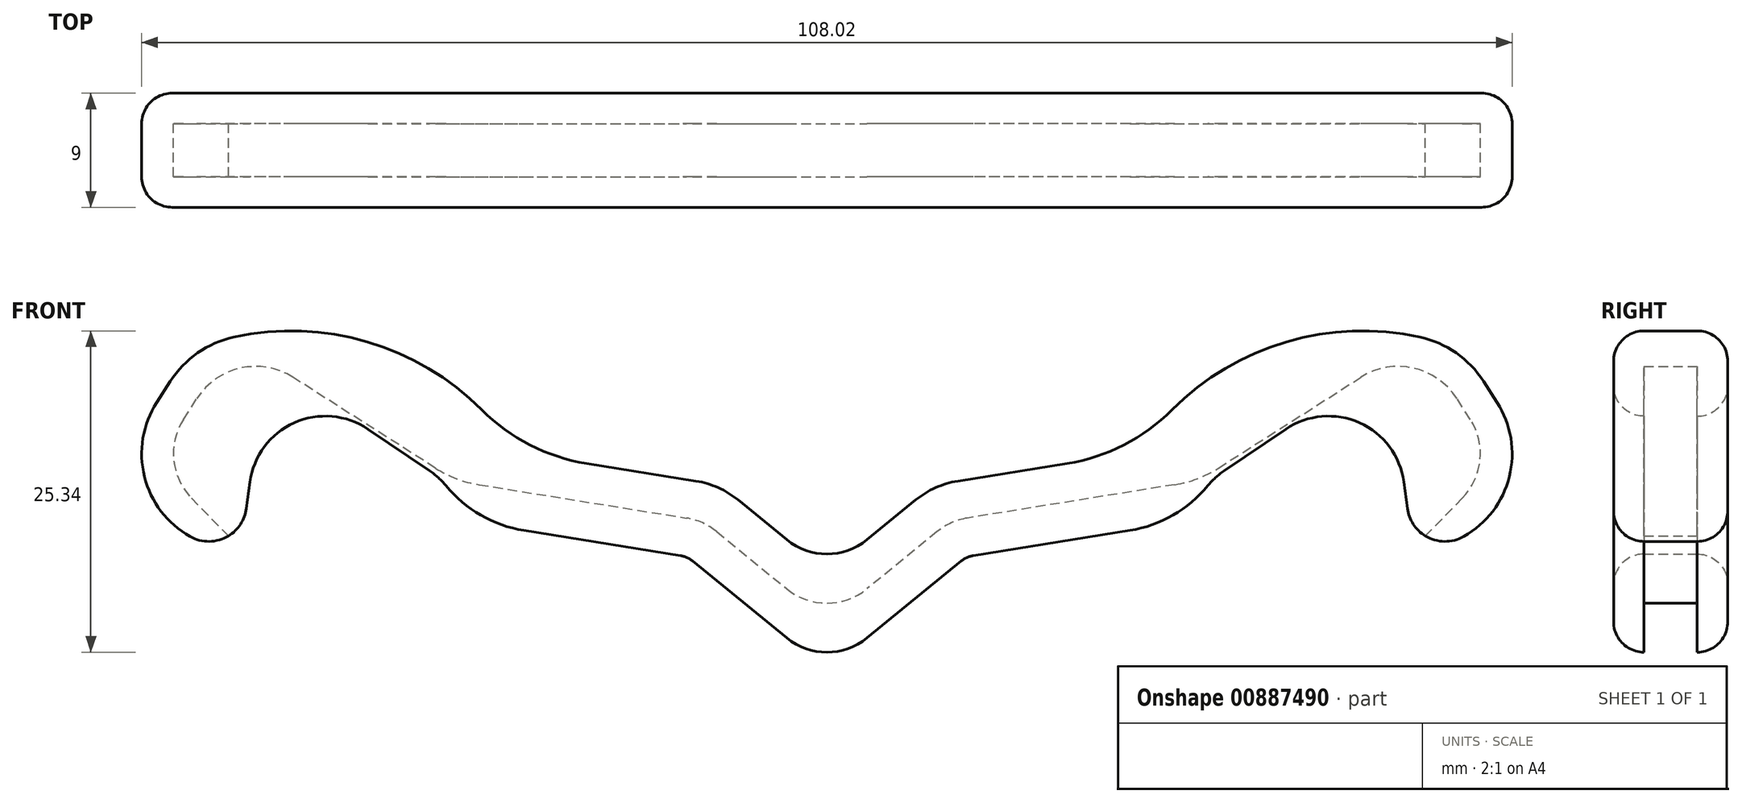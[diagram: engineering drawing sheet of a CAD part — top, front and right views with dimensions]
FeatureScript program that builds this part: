
annotation { "Feature Type Name" : "Feature", "Feature Type Description" : "" }
export const myFeature = defineFeature(function(context is Context, id is Id, definition is map)
    precondition{}
    {
        {
            var Q0;
            Q0=qCreatedBy(makeId("Front.planeOp"),FACE);
            var sketch = newSketch(context, id + "F0", { "sketchPlane" : qUnion([Q0])});
            skLineSegment(sketch, "E0.bottom", {"start": v(51.5, -38.63) * mm, "end": v(-51.5, -38.63) * mm, "construction": true});
            skLineSegment(sketch, "E0.top", {"start": v(51.5, 38.63) * mm, "end": v(-51.5, 38.63) * mm, "construction": true});
            skLineSegment(sketch, "E0.left", {"start": v(51.5, -38.63) * mm, "end": v(51.5, 38.63) * mm, "construction": true});
            skLineSegment(sketch, "E0.right", {"start": v(-51.5, -38.63) * mm, "end": v(-51.5, 38.63) * mm, "construction": true});
            skLineSegment(sketch, "E1", {"start": v(-50.1, 11.75) * mm, "end": v(-37.3, -1.35) * mm});
            skLineSegment(sketch, "E2", {"start": v(-22.41, -38.63) * mm, "end": v(-33.91, -6.75) * mm});
            skLineSegment(sketch, "E3", {"start": v(-30.84, 14.1) * mm, "end": v(-42.08, 21.26) * mm});
            skLineSegment(sketch, "E4", {"start": v(-27.43, 12.8) * mm, "end": v(-11.06, 10.17) * mm});
            skLineSegment(sketch, "E5", {"start": v(-8.7, 9.1) * mm, "end": v(-3.16, 4.6) * mm});
            skLineSegment(sketch, "E6", {"start": v(-50.72, 17.95) * mm, "end": v(-49.66, 19.6) * mm});
            skPoint(sketch, "E7.visualSharp", {"position": v(-9.74, 9.96) * mm});
            skArc(sketch, "E7.filletArc", {"start": v(-8.7, 9.1) * mm, "mid": v(-9.81, 9.8) * mm, "end": v(-11.06, 10.17) * mm});
            skPoint(sketch, "E8.visualSharp", {"position": v(-29.27, 13.1) * mm});
            skArc(sketch, "E8.filletArc", {"start": v(-30.84, 14.1) * mm, "mid": v(-29.2, 13.28) * mm, "end": v(-27.43, 12.8) * mm});
            skPoint(sketch, "E9.visualSharp", {"position": v(-52.87, 14.6) * mm});
            skArc(sketch, "E9.filletArc", {"start": v(-50.72, 17.95) * mm, "mid": v(-51.49, 14.74) * mm, "end": v(-50.1, 11.75) * mm});
            skPoint(sketch, "E10.visualSharp", {"position": v(-46.7, 24.21) * mm});
            skArc(sketch, "E10.filletArc", {"start": v(-42.08, 21.26) * mm, "mid": v(-46.21, 22) * mm, "end": v(-49.66, 19.6) * mm});
            skPoint(sketch, "E11.visualSharp", {"position": v(-35.02, -3.68) * mm});
            skArc(sketch, "E11.filletArc", {"start": v(-33.91, -6.75) * mm, "mid": v(-35.31, -3.87) * mm, "end": v(-37.3, -1.35) * mm});
            skCircle(sketch, "E12", {"center": v(-39.53, 12.21) * mm, "radius": 2 * mm});
            skCircle(sketch, "E13", {"center": v(-39.53, 12.21) * mm, "radius": 6 * mm});
            skPoint(sketch, "E14.visualSharp", {"position": v(-50.1, 11.75) * mm});
            skArc(sketch, "E15.0", {"start": v(-52.83, 19.3) * mm, "mid": v(-53.8, 13.44) * mm, "end": v(-50.21, 8.72) * mm});
            skLineSegment(sketch, "E15.1", {"start": v(-52.83, 19.3) * mm, "end": v(-51.76, 20.95) * mm});
            skArc(sketch, "E15.2", {"start": v(-40.73, 23.37) * mm, "mid": v(-46.75, 24.44) * mm, "end": v(-51.76, 20.95) * mm});
            skLineSegment(sketch, "E15.3", {"start": v(-29.5, 16.2) * mm, "end": v(-40.73, 23.37) * mm});
            skLineSegment(sketch, "E15.4", {"start": v(-7, 11.6) * mm, "end": v(-3.16, 8.46) * mm});
            skLineSegment(sketch, "E15.6", {"start": v(-18.95, 14.48) * mm, "end": v(-10.32, 13.1) * mm});
            skArc(sketch, "E15.7", {"start": v(-29.5, 16.2) * mm, "mid": v(-27.08, 15.28) * mm, "end": v(-24.49, 15.37) * mm});
            skArc(sketch, "E16", {"start": v(-27.2, 18.7) * mm, "mid": v(-36.23, 24.08) * mm, "end": v(-46.75, 24.44) * mm});
            skPoint(sketch, "E17.visualSharp", {"position": v(-24.49, 15.37) * mm});
            skArc(sketch, "E17.filletArc", {"start": v(-27.2, 18.7) * mm, "mid": v(-23.4, 15.94) * mm, "end": v(-18.95, 14.48) * mm});
            skLineSegment(sketch, "E18", {"start": v(-45.76, 10.93) * mm, "end": v(-45.48, 13) * mm});
            skPoint(sketch, "E19.visualSharp", {"position": v(-46.18, 7.75) * mm});
            skArc(sketch, "E19.filletArc", {"start": v(-50.21, 8.72) * mm, "mid": v(-47.4, 8.64) * mm, "end": v(-45.76, 10.93) * mm});
            skPoint(sketch, "E20.MirrorP", {"position": v(0, 0) * mm});
            skCircle(sketch, "E21", {"center": v(-34.67, 8.92) * mm, "radius": 2 * mm, "construction": true});
            skCircle(sketch, "E22", {"center": v(-34.67, 8.92) * mm, "radius": 6 * mm});
            skLineSegment(sketch, "E23", {"start": v(-36.17, 17.18) * mm, "end": v(-31.3, 13.9) * mm});
            skLineSegment(sketch, "E24.0", {"start": v(-10.6, 6.78) * mm, "end": v(-3.16, 0.72) * mm});
            skArc(sketch, "E24.1", {"start": v(-10.6, 6.78) * mm, "mid": v(-11.04, 7.06) * mm, "end": v(-11.54, 7.2) * mm});
            skLineSegment(sketch, "E24.2", {"start": v(-28.76, 9.98) * mm, "end": v(-11.54, 7.2) * mm});
            skArc(sketch, "E25", {"start": v(-30.03, 12.73) * mm, "mid": v(-27.28, 10.4) * mm, "end": v(-23.89, 9.2) * mm});
            skPoint(sketch, "E26.visualSharp", {"position": v(-8.47, 12.8) * mm});
            skArc(sketch, "E26.filletArc", {"start": v(-7, 11.6) * mm, "mid": v(-8.57, 12.57) * mm, "end": v(-10.32, 13.1) * mm});
            skLineSegment(sketch, "E27.MirrorCS", {"start": v(52.83, 19.3) * mm, "end": v(51.76, 20.95) * mm});
            skArc(sketch, "E28.MirrorCS", {"start": v(10.6, 6.78) * mm, "mid": v(11.04, 7.06) * mm, "end": v(11.54, 7.2) * mm});
            skLineSegment(sketch, "E29.MirrorCS", {"start": v(50.72, 17.95) * mm, "end": v(49.66, 19.6) * mm});
            skArc(sketch, "E30.MirrorCS", {"start": v(7, 11.6) * mm, "mid": v(8.57, 12.57) * mm, "end": v(10.32, 13.1) * mm});
            skArc(sketch, "E31.MirrorCS", {"start": v(8.7, 9.1) * mm, "mid": v(9.81, 9.8) * mm, "end": v(11.06, 10.17) * mm});
            skLineSegment(sketch, "E32.MirrorCS", {"start": v(45.76, 10.93) * mm, "end": v(45.48, 13) * mm});
            skArc(sketch, "E33.MirrorCS", {"start": v(33.91, -6.75) * mm, "mid": v(35.31, -3.87) * mm, "end": v(37.3, -1.35) * mm});
            skArc(sketch, "E34.MirrorCS", {"start": v(30.84, 14.1) * mm, "mid": v(29.2, 13.28) * mm, "end": v(27.43, 12.8) * mm});
            skLineSegment(sketch, "E35.MirrorCS", {"start": v(30.84, 14.1) * mm, "end": v(42.08, 21.26) * mm});
            skLineSegment(sketch, "E36.MirrorCS", {"start": v(28.76, 9.98) * mm, "end": v(11.54, 7.2) * mm});
            skLineSegment(sketch, "E37.MirrorCS", {"start": v(36.17, 17.18) * mm, "end": v(31.3, 13.9) * mm});
            skArc(sketch, "E38.MirrorCS", {"start": v(50.21, 8.72) * mm, "mid": v(47.4, 8.64) * mm, "end": v(45.76, 10.93) * mm});
            skPoint(sketch, "E39.MirrorP", {"position": v(52.87, 14.6) * mm});
            skArc(sketch, "E40.MirrorCS", {"start": v(50.72, 17.95) * mm, "mid": v(51.49, 14.74) * mm, "end": v(50.1, 11.75) * mm});
            skLineSegment(sketch, "E41.MirrorCS", {"start": v(50.1, 11.75) * mm, "end": v(37.3, -1.35) * mm});
            skPoint(sketch, "E42.MirrorP", {"position": v(9.74, 9.96) * mm});
            skArc(sketch, "E43.MirrorCS", {"start": v(29.5, 16.2) * mm, "mid": v(27.08, 15.28) * mm, "end": v(24.49, 15.37) * mm});
            skPoint(sketch, "E44.MirrorP", {"position": v(24.49, 15.37) * mm});
            skLineSegment(sketch, "E45.MirrorCS", {"start": v(27.43, 12.8) * mm, "end": v(11.06, 10.17) * mm});
            skArc(sketch, "E46.MirrorCS", {"start": v(52.83, 19.3) * mm, "mid": v(53.8, 13.44) * mm, "end": v(50.21, 8.72) * mm});
            skCircle(sketch, "E47.MirrorC", {"center": v(34.67, 8.92) * mm, "radius": 6 * mm});
            skLineSegment(sketch, "E48.MirrorCS", {"start": v(29.5, 16.2) * mm, "end": v(40.73, 23.37) * mm});
            skPoint(sketch, "E49.MirrorP", {"position": v(29.27, 13.1) * mm});
            skPoint(sketch, "E50.MirrorP", {"position": v(35.02, -3.68) * mm});
            skPoint(sketch, "E51.MirrorP", {"position": v(46.18, 7.75) * mm});
            skArc(sketch, "E52.MirrorCS", {"start": v(27.2, 18.7) * mm, "mid": v(36.23, 24.08) * mm, "end": v(46.75, 24.44) * mm});
            skPoint(sketch, "E53.MirrorP", {"position": v(8.47, 12.8) * mm});
            skCircle(sketch, "E54.MirrorC", {"center": v(39.53, 12.21) * mm, "radius": 2 * mm});
            skArc(sketch, "E55.MirrorCS", {"start": v(42.08, 21.26) * mm, "mid": v(46.21, 22) * mm, "end": v(49.66, 19.6) * mm});
            skPoint(sketch, "E56.MirrorP", {"position": v(50.1, 11.75) * mm});
            skLineSegment(sketch, "E57.MirrorCS", {"start": v(18.95, 14.48) * mm, "end": v(10.32, 13.1) * mm});
            skLineSegment(sketch, "E58.MirrorCS", {"start": v(10.6, 6.78) * mm, "end": v(3.16, 0.72) * mm});
            skCircle(sketch, "E59.MirrorC", {"center": v(34.67, 8.92) * mm, "radius": 2 * mm, "construction": true});
            skArc(sketch, "E60.MirrorCS", {"start": v(30.03, 12.73) * mm, "mid": v(27.28, 10.4) * mm, "end": v(23.89, 9.2) * mm});
            skLineSegment(sketch, "E61.MirrorCS", {"start": v(7, 11.6) * mm, "end": v(3.16, 8.46) * mm});
            skLineSegment(sketch, "E62.MirrorCS", {"start": v(8.7, 9.1) * mm, "end": v(3.16, 4.6) * mm});
            skPoint(sketch, "E63.MirrorP", {"position": v(46.7, 24.21) * mm});
            skCircle(sketch, "E64.MirrorC", {"center": v(39.53, 12.21) * mm, "radius": 6 * mm});
            skArc(sketch, "E65.MirrorCS", {"start": v(27.2, 18.7) * mm, "mid": v(23.4, 15.94) * mm, "end": v(18.95, 14.48) * mm});
            skArc(sketch, "E66.MirrorCS", {"start": v(40.73, 23.37) * mm, "mid": v(46.75, 24.44) * mm, "end": v(51.76, 20.95) * mm});
            skPoint(sketch, "E67.visualSharp", {"position": v(0, 5.88) * mm});
            skArc(sketch, "E67.filletArc", {"start": v(-3.16, 8.46) * mm, "mid": v(0, 7.34) * mm, "end": v(3.16, 8.46) * mm});
            skPoint(sketch, "E68.visualSharp", {"position": v(0, 2.01) * mm});
            skArc(sketch, "E68.filletArc", {"start": v(-3.16, 4.6) * mm, "mid": v(0, 3.47) * mm, "end": v(3.16, 4.6) * mm});
            skPoint(sketch, "E69.visualSharp", {"position": v(0, -1.86) * mm});
            skArc(sketch, "E69.filletArc", {"start": v(-3.16, 0.72) * mm, "mid": v(0, -0.4) * mm, "end": v(3.16, 0.72) * mm});
            skSolve(sketch);
        }
        {
            var Q0;
            Q0=makeQuery(id+"F0.imprint","IMPRINT",FACE,{"disambiguationData":[TD([[makeQuery(id+"F0.imprint","IMPRINT",EDGE,{"derivedFrom":sQuery(id+"F0.wireOp",EDGE,"E3")}),-1.0]])]});
            extrude(context, id + "F1", {"entities" : qUnion([Q0]), "depth" : 9 * mm, "offsetDistance" : 25 * mm, "symmetric" : true});
        }
        {
            var Q0;
            Q0=makeQuery(id+"F0.imprint","IMPRINT",FACE,{"disambiguationData":[TD([[makeQuery(id+"F0.imprint","IMPRINT",EDGE,{"derivedFrom":sQuery(id+"F0.wireOp",EDGE,"E3")}),1.0]])]});
            extrude(context, id + "F2", {"entities" : qUnion([Q0]), "depth" : 4.5 * mm, "offsetDistance" : 25 * mm, "hasSecondDirection" : true, "secondDirectionOppositeDirection" : false, "secondDirectionDepth" : 2.1 * mm});
        }
        {
            var Q0;
            Q0=makeQuery(id+"F2.opExtrude","SWEPT_BODY",BODY,{"disambiguationData":[OSD([sQuery(id+"F0.wireOp",EDGE,"E1"),sQuery(id+"F0.wireOp",EDGE,"E3"),sQuery(id+"F0.wireOp",EDGE,"E4"),sQuery(id+"F0.wireOp",EDGE,"E5"),sQuery(id+"F0.wireOp",EDGE,"E6"),sQuery(id+"F0.wireOp",EDGE,"E7.filletArc"),sQuery(id+"F0.wireOp",EDGE,"E8.filletArc"),sQuery(id+"F0.wireOp",EDGE,"E9.filletArc"),sQuery(id+"F0.wireOp",EDGE,"E10.filletArc"),sQuery(id+"F0.wireOp",EDGE,"E13"),sQuery(id+"F0.wireOp",EDGE,"f1af8404-0ecc-4397-b0ce-8625b56a2dd6.1"),sQuery(id+"F0.wireOp",EDGE,"f1af8404-0ecc-4397-b0ce-8625b56a2dd6.2"),sQuery(id+"F0.wireOp",EDGE,"f1af8404-0ecc-4397-b0ce-8625b56a2dd6.3"),sQuery(id+"F0.wireOp",EDGE,"f1af8404-0ecc-4397-b0ce-8625b56a2dd6.4"),sQuery(id+"F0.wireOp",EDGE,"mf33vLFF-kvHl-AOLd-bRcb-veGphdkbE9sc"),sQuery(id+"F0.wireOp",EDGE,"E18"),sQuery(id+"F0.wireOp",EDGE,"E19.filletArc"),sQuery(id+"F0.wireOp",EDGE,"fe010fde-2d3e-4c62-8526-f0e82fc0f9a31.MirrorCS"),sQuery(id+"F0.wireOp",EDGE,"fe010fde-2d3e-4c62-8526-f0e82fc0f9a34.MirrorCS"),sQuery(id+"F0.wireOp",EDGE,"fe010fde-2d3e-4c62-8526-f0e82fc0f9a35.MirrorCS"),sQuery(id+"F0.wireOp",EDGE,"fe010fde-2d3e-4c62-8526-f0e82fc0f9a37.MirrorCS"),sQuery(id+"F0.wireOp",EDGE,"fe010fde-2d3e-4c62-8526-f0e82fc0f9a38.MirrorCS"),sQuery(id+"F0.wireOp",EDGE,"fe010fde-2d3e-4c62-8526-f0e82fc0f9a39.MirrorCS"),sQuery(id+"F0.wireOp",EDGE,"fe010fde-2d3e-4c62-8526-f0e82fc0f9a311.MirrorCS"),sQuery(id+"F0.wireOp",EDGE,"fe010fde-2d3e-4c62-8526-f0e82fc0f9a314.MirrorCS"),sQuery(id+"F0.wireOp",EDGE,"fe010fde-2d3e-4c62-8526-f0e82fc0f9a316.MirrorCS"),sQuery(id+"F0.wireOp",EDGE,"fe010fde-2d3e-4c62-8526-f0e82fc0f9a320.MirrorCS"),sQuery(id+"F0.wireOp",EDGE,"fe010fde-2d3e-4c62-8526-f0e82fc0f9a321.MirrorCS"),sQuery(id+"F0.wireOp",EDGE,"fe010fde-2d3e-4c62-8526-f0e82fc0f9a322.MirrorCS"),sQuery(id+"F0.wireOp",EDGE,"fe010fde-2d3e-4c62-8526-f0e82fc0f9a325.MirrorCS"),sQuery(id+"F0.wireOp",EDGE,"fe010fde-2d3e-4c62-8526-f0e82fc0f9a327.MirrorCS"),sQuery(id+"F0.wireOp",EDGE,"fe010fde-2d3e-4c62-8526-f0e82fc0f9a329.MirrorC"),sQuery(id+"F0.wireOp",EDGE,"fe010fde-2d3e-4c62-8526-f0e82fc0f9a330.MirrorCS"),sQuery(id+"F0.wireOp",EDGE,"fe010fde-2d3e-4c62-8526-f0e82fc0f9a336.MirrorCS"),sQuery(id+"F0.wireOp",EDGE,"871c2d67-10a7-44d1-9577-ba048edcbc6e.filletArc"),sQuery(id+"F0.wireOp",EDGE,"47416115-70ee-42ff-94e8-e02ab53c1f6f.filletArc")])]});
            var Q1;
            Q1=qCreatedBy(makeId("Front.planeOp"),FACE);
            mirror(context, id + "F3", {"operationType" : NewBodyOperationType.ADD, "entities" : qUnion([Q0]), "mirrorPlane" : qUnion([Q1])});
        }
        {
            var Q0;
            Q0=makeQuery(id+"F1.opExtrude","CAP_EDGE",EDGE,{"disambiguationData":[OSD([sQuery(id+"F0.wireOp",EDGE,"E67.filletArc")])],"isStart":false});
            var Q1;
            Q1=makeQuery(id+"F1.opExtrude","CAP_EDGE",EDGE,{"disambiguationData":[OSD([sQuery(id+"F0.wireOp",EDGE,"E67.filletArc")])],"isStart":true});
            fillet(context, id + "F4", {"entities" : qUnion([Q0, Q1]), "radius" : 2.4 * mm, "tangentPropagation" : true, "allowEdgeOverflow" : false});
        }
    });
